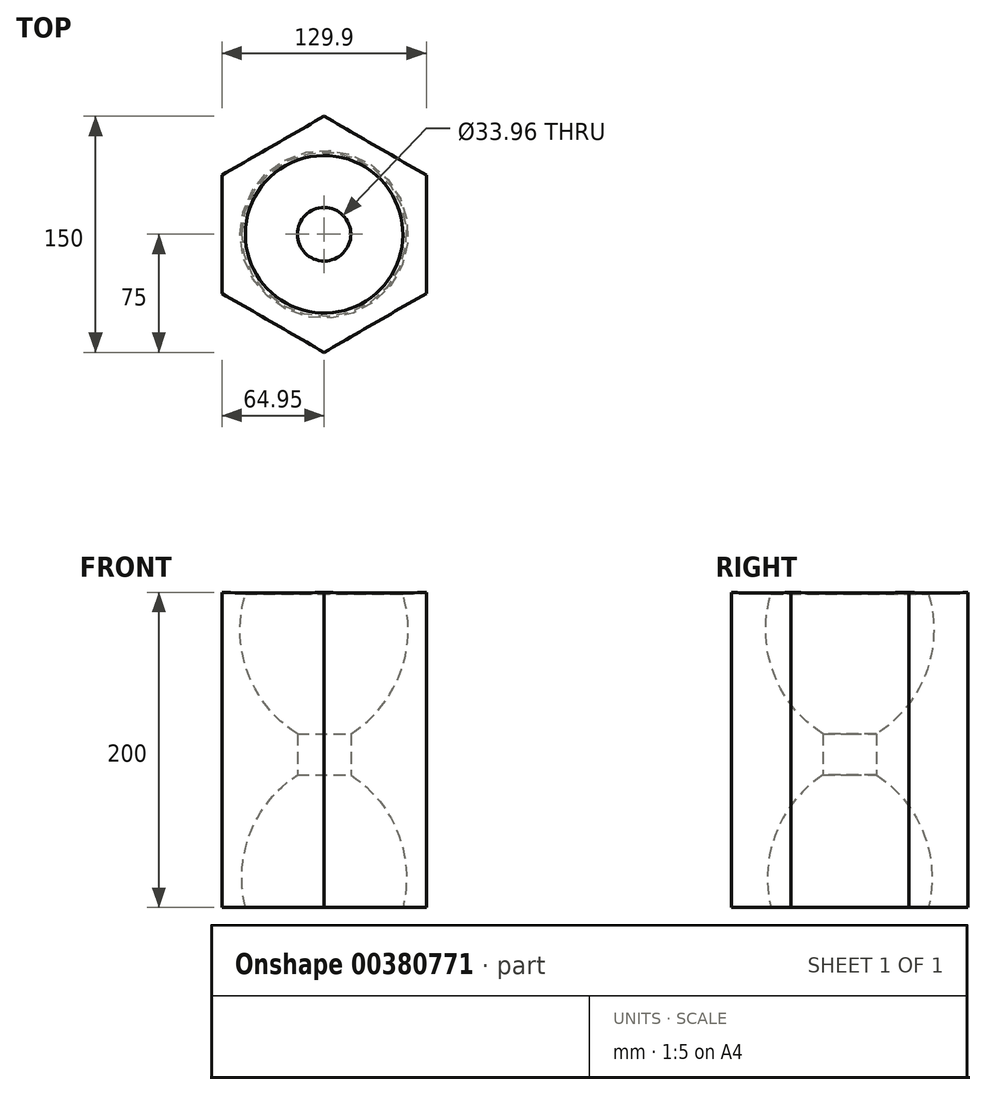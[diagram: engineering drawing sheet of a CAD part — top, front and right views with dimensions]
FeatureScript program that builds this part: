
annotation { "Feature Type Name" : "Feature", "Feature Type Description" : "" }
export const myFeature = defineFeature(function(context is Context, id is Id, definition is map)
    precondition{}
    {
        {
            var Q0;
            Q0=qCreatedBy(makeId("Front.planeOp"),FACE);
            var sketch = newSketch(context, id + "F0", { "sketchPlane" : qUnion([Q0])});
            skLineSegment(sketch, "E0", {"start": v(0, 0) * mm, "end": v(0, 85.36) * mm});
            skLineSegment(sketch, "E1", {"start": v(50, 0) * mm, "end": v(75, 0) * mm});
            skArc(sketch, "E2", {"start": v(50, 0) * mm, "mid": v(46.83, 47.27) * mm, "end": v(16.98, 84.06) * mm});
            skLineSegment(sketch, "E3", {"start": v(16.98, 84.06) * mm, "end": v(16.98, 110.17) * mm});
            skLineSegment(sketch, "E4", {"start": v(75, 0) * mm, "end": v(75, 200) * mm});
            skLineSegment(sketch, "E5", {"start": v(75, 200) * mm, "end": v(75, 200) * mm});
            skLineSegment(sketch, "E6", {"start": v(50.02, 198.98) * mm, "end": v(75, 200) * mm});
            skArc(sketch, "E7", {"start": v(16.98, 110.17) * mm, "mid": v(48.46, 149.01) * mm, "end": v(50.02, 198.98) * mm});
            skSolve(sketch);
        }
        {
            var Q0;
            Q0=makeQuery(id+"F0.imprint","IMPRINT",FACE,{"disambiguationData":[TD([[makeQuery(id+"F0.imprint","IMPRINT",EDGE,{"derivedFrom":sQuery(id+"F0.wireOp",EDGE,"E1")}),1.0]])]});
            var Q1;
            Q1=sQuery(id+"F0.wireOp",EDGE,"E0");
            revolve(context, id + "F1", {"entities" : qUnion([Q0]), "axis" : qUnion([Q1]), "revolveType" : RevolveType.FULL});
        }
        {
            var Q0;
            Q0=qCreatedBy(makeId("Top.planeOp"),FACE);
            var sketch = newSketch(context, id + "F2", { "sketchPlane" : qUnion([Q0])});
            skCircle(sketch, "E8.cCircle", {"center": v(0, 0) * mm, "radius": 75 * mm, "construction": true});
            skLineSegment(sketch, "E8.0", {"start": v(-64.95, -37.5) * mm, "end": v(-64.95, 37.5) * mm});
            skLineSegment(sketch, "E8.1", {"start": v(-64.95, 37.5) * mm, "end": v(0, 75) * mm});
            skLineSegment(sketch, "E8.2", {"start": v(0, 75) * mm, "end": v(64.95, 37.5) * mm});
            skLineSegment(sketch, "E8.3", {"start": v(64.95, 37.5) * mm, "end": v(64.95, -37.5) * mm});
            skLineSegment(sketch, "E8.4", {"start": v(64.95, -37.5) * mm, "end": v(0, -75) * mm});
            skLineSegment(sketch, "E8.5", {"start": v(0, -75) * mm, "end": v(-64.95, -37.5) * mm});
            skSolve(sketch);
        }
        {
            var Q0;
            Q0 = qSketchRegion(id + "F2", true);
            extrude(context, id + "F3", {"entities" : qUnion([Q0]), "operationType" : NewBodyOperationType.INTERSECT, "depth" : 206.62 * mm});
        }
    });
